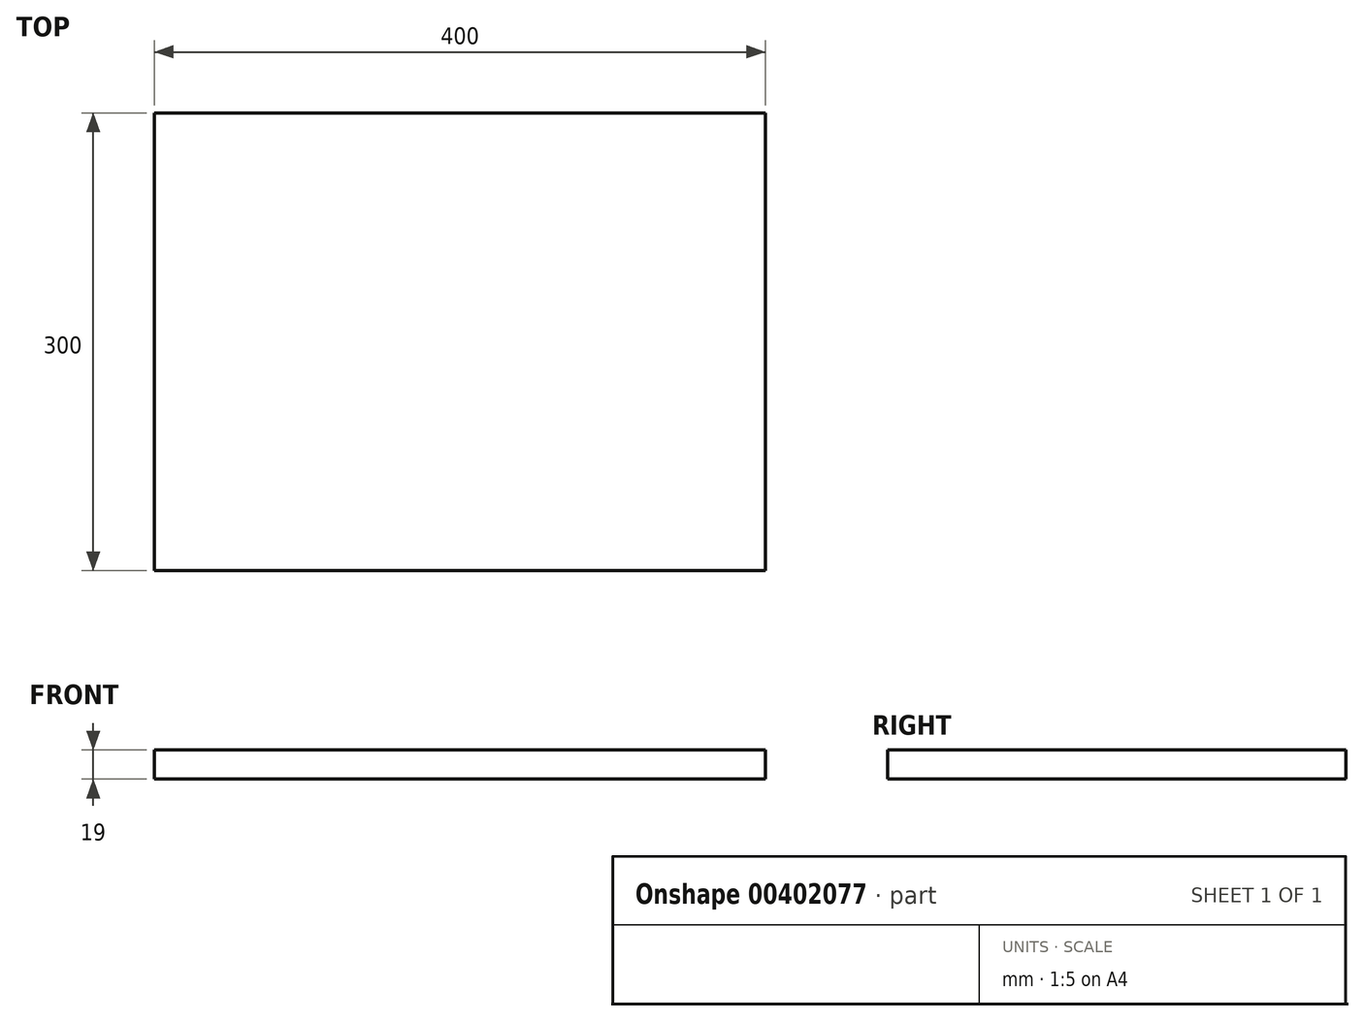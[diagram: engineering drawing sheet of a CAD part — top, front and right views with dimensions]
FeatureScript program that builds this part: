
annotation { "Feature Type Name" : "Feature", "Feature Type Description" : "" }
export const myFeature = defineFeature(function(context is Context, id is Id, definition is map)
    precondition{}
    {
        {
            var Q0;
            Q0=qCreatedBy(makeId("Top.planeOp"),FACE);
            var sketch = newSketch(context, id + "F0", { "sketchPlane" : qUnion([Q0])});
            skLineSegment(sketch, "E0.bottom", {"start": v(0, 0) * mm, "end": v(400, 0) * mm});
            skLineSegment(sketch, "E0.top", {"start": v(0, 300) * mm, "end": v(400, 300) * mm});
            skLineSegment(sketch, "E0.left", {"start": v(0, 0) * mm, "end": v(0, 300) * mm});
            skLineSegment(sketch, "E0.right", {"start": v(400, 0) * mm, "end": v(400, 300) * mm});
            skSolve(sketch);
        }
        {
            var Q0;
            Q0=qSketchRegion(id+"F0",true);
            extrude(context, id + "F1", {"entities" : qUnion([Q0]), "depth" : 19 * mm});
        }
    });
